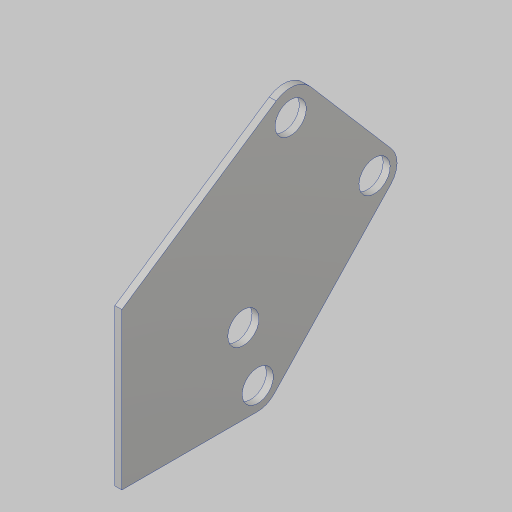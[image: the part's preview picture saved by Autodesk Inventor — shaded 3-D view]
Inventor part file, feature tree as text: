
AUTODESK INVENTOR PART (.ipt)
format: ipt  version: 2023.5 (Build 275446000, 446)  size: 150,016 bytes
history: native  units: in
note: dims shown in document units (in); Inventor stores cm internally (conversion verified against a paired STEP export)
features: sketch x2, extrude x1
ambient origin geometry x8: Origin, YZ Plane, XZ Plane, XY Plane, X Axis, Y Axis, Z Axis, Center Point
bodies: Solid1 (feature_tree)
feature tree (3):
  sketch  "Sketch1"  dims[d0=2.0in d1=16.0in]
  extrude  "Extrusion1"  Depth=16.0in
  sketch  "Sketch2"  dims[d2=0.75in d3=5.75in d4=3.0in d5=1.375in d6=4.5in d7=0.5in d8=1.375in d9=0.9375in d10=2.0in d11=1.375in d12=2.126in d13=3.0in d14=4.5in d15=3.0in d16=4.5in d17=0.25in d18=2.0in d19=0.25in d20=0.25in d21=4.5in d22=4.4882in d23=5.375in d24=1.125in d27=0.375in d28=0.25in d29=0.25in d30=0.375in d31=0.25in d32=0.0in d33=0.5in d34=0.0344in]
